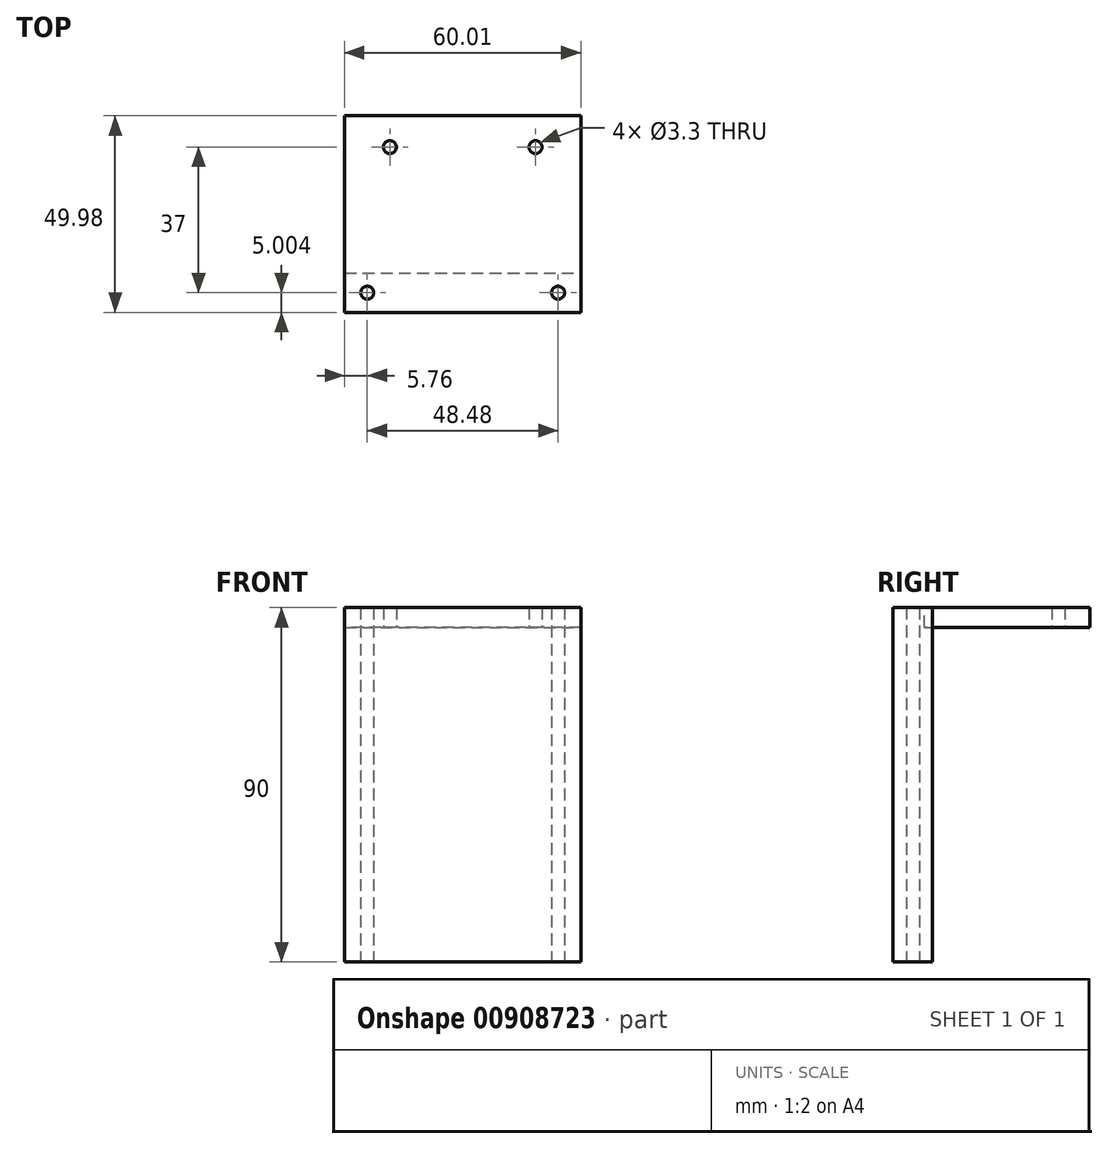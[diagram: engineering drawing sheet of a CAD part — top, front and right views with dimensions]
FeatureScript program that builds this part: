
annotation { "Feature Type Name" : "Feature", "Feature Type Description" : "" }
export const myFeature = defineFeature(function(context is Context, id is Id, definition is map)
    precondition{}
    {
        {
            var Q0;
            Q0=qCreatedBy(makeId("Top.planeOp"),FACE);
            var sketch = newSketch(context, id + "F0", { "sketchPlane" : qUnion([Q0])});
            skLineSegment(sketch, "E0.top", {"start": v(10.01, -7.98) * mm, "end": v(-49.99, -7.98) * mm});
            skLineSegment(sketch, "E1", {"start": v(-20, 34.02) * mm, "end": v(-38.5, 34.02) * mm, "construction": true});
            skLineSegment(sketch, "E2", {"start": v(-20, 34.02) * mm, "end": v(-1.5, 34.02) * mm, "construction": true});
            skCircle(sketch, "E3", {"center": v(-38.5, 34.02) * mm, "radius": 1.65 * mm});
            skCircle(sketch, "E4", {"center": v(-1.5, 34.02) * mm, "radius": 1.65 * mm});
            skCircle(sketch, "E5", {"center": v(4.24, -2.98) * mm, "radius": 1.65 * mm});
            skCircle(sketch, "E6", {"center": v(-44.24, -2.98) * mm, "radius": 1.65 * mm});
            skLineSegment(sketch, "E7", {"start": v(-20, 34.02) * mm, "end": v(-20, -7.98) * mm, "construction": true});
            skPoint(sketch, "E7.endSnap0", {"position": v(-20, 2.02) * mm});
            skLineSegment(sketch, "E8", {"start": v(-20, -7.98) * mm, "end": v(-20, 34.02) * mm, "construction": true});
            skLineSegment(sketch, "E9", {"start": v(10.01, -7.98) * mm, "end": v(10.01, 2.02) * mm});
            skLineSegment(sketch, "E10", {"start": v(-49.99, -7.98) * mm, "end": v(-49.99, 2.02) * mm});
            skLineSegment(sketch, "E11", {"start": v(-49.99, 2.02) * mm, "end": v(10.01, 2.02) * mm});
            skLineSegment(sketch, "E12.top", {"start": v(10.01, 2.02) * mm, "end": v(-49.99, 2.02) * mm});
            skSolve(sketch);
        }
        {
            var Q0;
            Q0=qCreatedBy(makeId("Front.planeOp"),FACE);
            var sketch = newSketch(context, id + "F1", { "sketchPlane" : qUnion([Q0])});
            skLineSegment(sketch, "E13", {"start": v(0, 0) * mm, "end": v(0, 68.75) * mm, "construction": true});
            skLineSegment(sketch, "E14.bottom", {"start": v(10, 85) * mm, "end": v(-50, 85) * mm});
            skLineSegment(sketch, "E14.top", {"start": v(10, 90) * mm, "end": v(-50, 90) * mm});
            skLineSegment(sketch, "E14.left", {"start": v(10, 85) * mm, "end": v(10, 90) * mm});
            skLineSegment(sketch, "E14.right", {"start": v(-50, 85) * mm, "end": v(-50, 90) * mm});
            skSolve(sketch);
        }
        {
            var Q0;
            {var subQ1=sQuery(id+"F0.wireOp",EDGE,"E0.top");Q0=makeQuery(id+"F0.imprint","IMPRINT",FACE,{"disambiguationData":[TD([[makeQuery(id+"F0.imprint","IMPRINT",EDGE,{"derivedFrom":subQ1}),-1.0]])]});}
            extrude(context, id + "F2", {"entities" : qUnion([Q0]), "depth" : 90 * mm, "offsetDistance" : 25 * mm});
        }
        {
            var Q0;
            Q0 = qSketchRegion(id + "F1", true);
            extrude(context, id + "F3", {"entities" : qUnion([Q0]), "operationType" : NewBodyOperationType.ADD, "oppositeDirection" : true, "depth" : 42 * mm, "offsetDistance" : 25 * mm});
        }
        {
            var Q0;
            Q0=makeQuery(id+"F0.imprint","IMPRINT",FACE,{"disambiguationData":[TD([[makeQuery(id+"F0.imprint","IMPRINT",EDGE,{"derivedFrom":sQuery(id+"F0.wireOp",EDGE,"E5")}),1.0]])]});
            var Q1;
            Q1=makeQuery(id+"F0.imprint","IMPRINT",FACE,{"disambiguationData":[TD([[makeQuery(id+"F0.imprint","IMPRINT",EDGE,{"derivedFrom":sQuery(id+"F0.wireOp",EDGE,"E6")}),1.0]])]});
            var Q2;
            Q2=makeQuery(id+"F0.imprint","IMPRINT",FACE,{"disambiguationData":[TD([[makeQuery(id+"F0.imprint","IMPRINT",EDGE,{"derivedFrom":sQuery(id+"F0.wireOp",EDGE,"E3")}),1.0]])]});
            var Q3;
            Q3=makeQuery(id+"F0.imprint","IMPRINT",FACE,{"disambiguationData":[TD([[makeQuery(id+"F0.imprint","IMPRINT",EDGE,{"derivedFrom":sQuery(id+"F0.wireOp",EDGE,"E4")}),1.0]])]});
            extrude(context, id + "F4", {"entities" : qUnion([Q0, Q1, Q2, Q3]), "operationType" : NewBodyOperationType.REMOVE, "depth" : 97 * mm, "offsetDistance" : 25 * mm});
        }
    });
